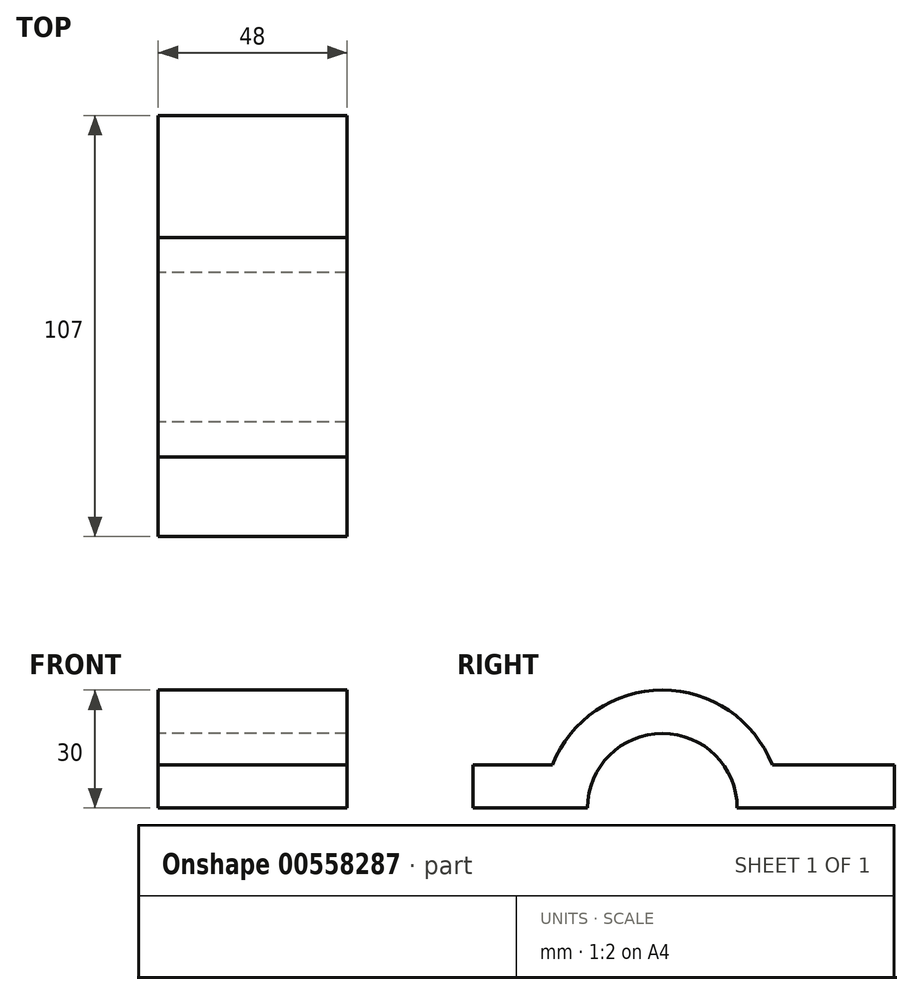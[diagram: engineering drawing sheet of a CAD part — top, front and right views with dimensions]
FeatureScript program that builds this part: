
annotation { "Feature Type Name" : "Feature", "Feature Type Description" : "" }
export const myFeature = defineFeature(function(context is Context, id is Id, definition is map)
    precondition{}
    {
        {
            var Q0;
            Q0=qCreatedBy(makeId("Right.planeOp"),FACE);
            var sketch = newSketch(context, id + "F0", { "sketchPlane" : qUnion([Q0])});
            skCircle(sketch, "E0", {"center": v(0, 0) * mm, "radius": 30 * mm});
            skCircle(sketch, "E1", {"center": v(0, 0) * mm, "radius": 19 * mm});
            skLineSegment(sketch, "E2.bottom", {"start": v(-48.11, 0) * mm, "end": v(58.89, 0) * mm});
            skLineSegment(sketch, "E2.top", {"start": v(-48.11, 11) * mm, "end": v(58.89, 11) * mm});
            skLineSegment(sketch, "E2.left", {"start": v(-48.11, 0) * mm, "end": v(-48.11, 11) * mm});
            skLineSegment(sketch, "E2.right", {"start": v(58.89, 0) * mm, "end": v(58.89, 11) * mm});
            skLineSegment(sketch, "E3.bottom", {"start": v(47.89, 11) * mm, "end": v(58.89, 11) * mm});
            skLineSegment(sketch, "E3.top", {"start": v(47.89, 41) * mm, "end": v(58.89, 41) * mm});
            skLineSegment(sketch, "E3.left", {"start": v(47.89, 11) * mm, "end": v(47.89, 41) * mm});
            skLineSegment(sketch, "E3.right", {"start": v(58.89, 11) * mm, "end": v(58.89, 41) * mm});
            skSolve(sketch);
        }
        {
            var Q0;
            {var subQ5=sQuery(id+"F0.wireOp",EDGE,"E2.left");Q0=makeQuery(id+"F0.imprint","IMPRINT",FACE,{"disambiguationData":[TD([[makeQuery(id+"F0.imprint","IMPRINT",EDGE,{"derivedFrom":subQ5}),-1.0]])]});}
            var Q1;
            Q1=makeQuery(id+"F0.imprint","IMPRINT",FACE,{"disambiguationData":[TD([[makeQuery(id+"F0.imprint","IMPRINT",EDGE,{"derivedFrom":sQuery(id+"F0.wireOp",EDGE,"E3.bottom")}),1.0]])]});
            var Q2;
            {var subQ0=sQuery(id+"F0.wireOp",EDGE,"E2.right");Q2=makeQuery(id+"F0.imprint","IMPRINT",FACE,{"disambiguationData":[TD([[makeQuery(id+"F0.imprint","IMPRINT",EDGE,{"derivedFrom":subQ0}),1.0]])]});}
            var Q3;
            {var subQ0=sQuery(id+"F0.wireOp",EDGE,"E2.top");var subQ1=sQuery(id+"F0.wireOp",EDGE,"E0");var subQ2=makeQuery(id+"F0.imprint","INTERSECT",VERTEX,{"disambiguationData":[OD(0.0)],"derivedFrom":[subQ1,subQ0]});Q3=makeQuery(id+"F0.imprint","IMPRINT",FACE,{"disambiguationData":[TD([[makeQuery(id+"F0.imprint","IMPRINT",EDGE,{"disambiguationData":[TD([[subQ2,-1.0]])],"derivedFrom":subQ1}),1.0]])]});}
            var Q4;
            {var subQ0=sQuery(id+"F0.wireOp",EDGE,"E2.top");var subQ1=sQuery(id+"F0.wireOp",EDGE,"E0");var subQ2=makeQuery(id+"F0.imprint","INTERSECT",VERTEX,{"disambiguationData":[OD(0.0)],"derivedFrom":[subQ1,subQ0]});Q4=makeQuery(id+"F0.imprint","IMPRINT",FACE,{"disambiguationData":[TD([[makeQuery(id+"F0.imprint","IMPRINT",EDGE,{"disambiguationData":[TD([[subQ2,1.0]])],"derivedFrom":subQ1}),1.0]])]});}
            var Q5;
            {var subQ0=sQuery(id+"F0.wireOp",EDGE,"E2.top");var subQ1=sQuery(id+"F0.wireOp",EDGE,"E0");var subQ2=makeQuery(id+"F0.imprint","INTERSECT",VERTEX,{"disambiguationData":[OD(1.0)],"derivedFrom":[subQ1,subQ0]});Q5=makeQuery(id+"F0.imprint","IMPRINT",FACE,{"disambiguationData":[TD([[makeQuery(id+"F0.imprint","IMPRINT",EDGE,{"disambiguationData":[TD([[subQ2,-1.0]])],"derivedFrom":subQ1}),1.0]])]});}
            extrude(context, id + "F1", {"entities" : qUnion([Q0, Q1, Q2, Q3, Q4, Q5]), "endBound" : BoundingType.SYMMETRIC, "depth" : 48 * mm, "offsetDistance" : 25 * mm});
        }
        {
            var Q0;
            Q0=makeQuery(id+"F1.opExtrude","SWEPT_FACE",FACE,{"disambiguationData":[OSD([sQuery(id+"F0.wireOp",EDGE,"E2.right"),sQuery(id+"F0.wireOp",EDGE,"E3.right")])]});
            var sketch = newSketch(context, id + "F2", { "sketchPlane" : qUnion([Q0])});
            skLineSegment(sketch, "E4", {"start": v(0, 41) * mm, "end": v(0, 0) * mm, "construction": true});
            skCircle(sketch, "E5", {"center": v(0, 25) * mm, "radius": 6.5 * mm});
            skLineSegment(sketch, "E6", {"start": v(-6.5, 25) * mm, "end": v(-6.5, 41) * mm});
            skLineSegment(sketch, "E7", {"start": v(6.5, 25) * mm, "end": v(6.5, 41) * mm});
            skSolve(sketch);
        }
        {
            var Q0;
            {var subQ0=sQuery(id+"F2.wireOp",EDGE,"E6");Q0=makeQuery(id+"F2.imprint","IMPRINT",FACE,{"disambiguationData":[TD([[makeQuery(id+"F2.imprint","IMPRINT",EDGE,{"derivedFrom":subQ0}),-1.0]])]});}
            var Q1;
            {var subQ0=sQuery(id+"F2.wireOp",EDGE,"E5");var subQ3=makeQuery(id+"F2.imprint","IMPRINT",VERTEX,{"derivedFrom":subQ0});Q1=makeQuery(id+"F2.imprint","IMPRINT",FACE,{"disambiguationData":[TD([[makeQuery(id+"F2.imprint","IMPRINT",EDGE,{"disambiguationData":[TD([[subQ3,1.0]])],"derivedFrom":subQ0}),1.0]])]});}
            extrude(context, id + "F3", {"entities" : qUnion([Q0, Q1]), "operationType" : NewBodyOperationType.REMOVE, "oppositeDirection" : true, "depth" : 30.3 * mm, "offsetDistance" : 25 * mm});
        }
    });
